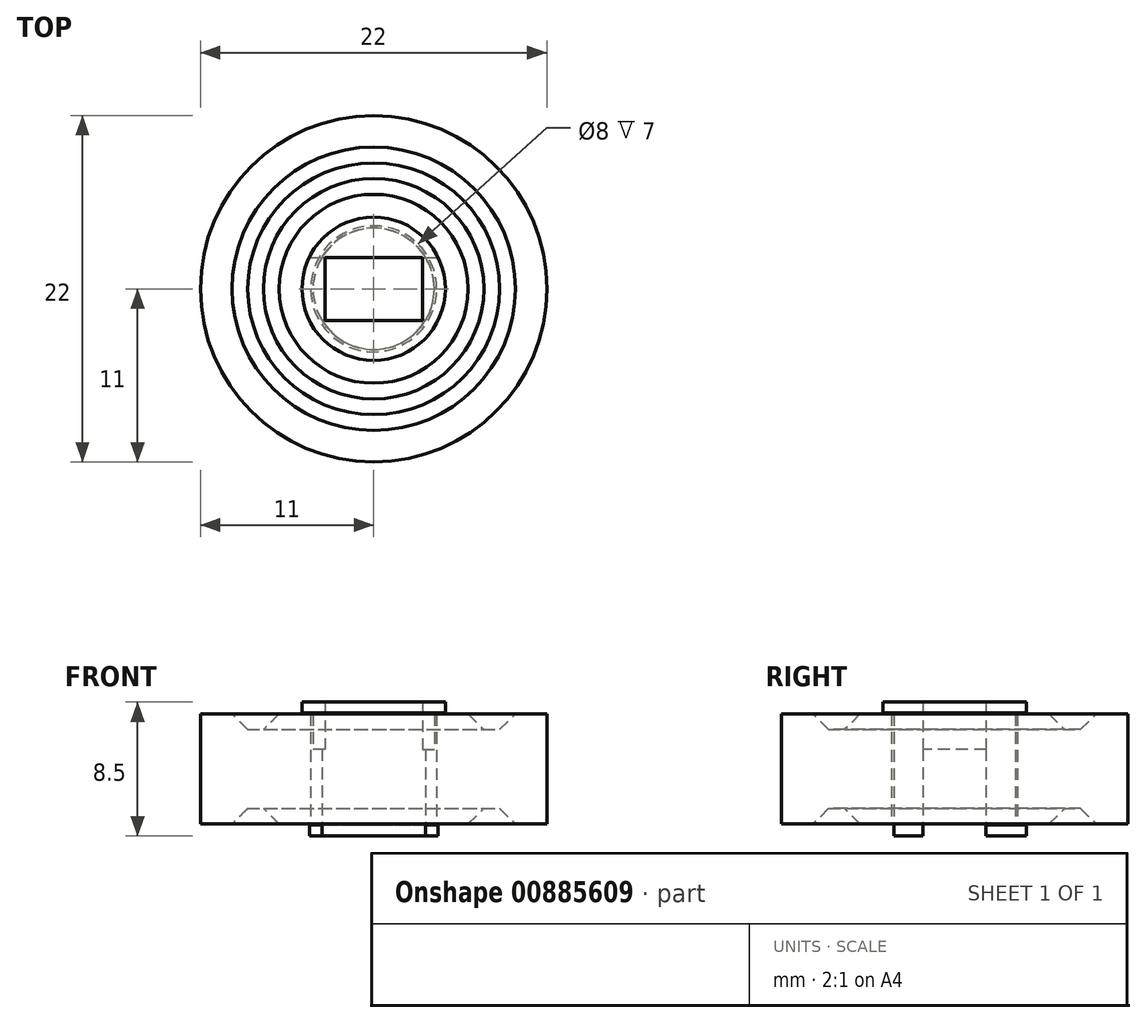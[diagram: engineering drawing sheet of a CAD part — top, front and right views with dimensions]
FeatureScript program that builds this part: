
annotation { "Feature Type Name" : "Feature", "Feature Type Description" : "" }
export const myFeature = defineFeature(function(context is Context, id is Id, definition is map)
    precondition{}
    {
        {
            assignVariable(context, id + "F0", {"name" : "bearing_thick", "anyValue" : 7});
        }
        {
            var Q0;
            Q0=qCreatedBy(makeId("Right.planeOp"),FACE);
            var sketch = newSketch(context, id + "F1", { "sketchPlane" : qUnion([Q0])});
            skLineSegment(sketch, "E0.bottom", {"start": v(-4, 0) * mm, "end": v(-11, 0) * mm});
            skLineSegment(sketch, "E0.top", {"start": v(-4, 3.5) * mm, "end": v(-6, 3.5) * mm});
            skLineSegment(sketch, "E0.left", {"start": v(-4, 0) * mm, "end": v(-4, 3.5) * mm});
            skLineSegment(sketch, "E0.right", {"start": v(-11, 0) * mm, "end": v(-11, 3.5) * mm});
            skLineSegment(sketch, "E1", {"start": v(-9, 3.5) * mm, "end": v(-8, 2.5) * mm});
            skLineSegment(sketch, "E2", {"start": v(-8, 2.5) * mm, "end": v(-7, 2.5) * mm});
            skLineSegment(sketch, "E3", {"start": v(-7, 2.5) * mm, "end": v(-6, 3.5) * mm});
            skLineSegment(sketch, "E4.MirrorCS", {"start": v(7, 2.5) * mm, "end": v(6, 3.5) * mm});
            skLineSegment(sketch, "E5.MirrorCS", {"start": v(4, 0) * mm, "end": v(4, 3.5) * mm});
            skLineSegment(sketch, "E6.MirrorCS", {"start": v(11, 0) * mm, "end": v(11, 3.5) * mm});
            skLineSegment(sketch, "E7.MirrorCS", {"start": v(9, 3.5) * mm, "end": v(8, 2.5) * mm});
            skLineSegment(sketch, "E8.MirrorCS", {"start": v(4, 0) * mm, "end": v(11, 0) * mm});
            skLineSegment(sketch, "E9.MirrorCS", {"start": v(4, 3.5) * mm, "end": v(6, 3.5) * mm});
            skLineSegment(sketch, "E10.MirrorCS", {"start": v(8, 2.5) * mm, "end": v(7, 2.5) * mm});
            skLineSegment(sketch, "E11.trimOffspring", {"start": v(-9, 3.5) * mm, "end": v(-11, 3.5) * mm});
            skLineSegment(sketch, "E12.trimOffspring", {"start": v(9, 3.5) * mm, "end": v(11, 3.5) * mm});
            skLineSegment(sketch, "E13", {"start": v(0, 0) * mm, "end": v(0, 4.43) * mm});
            skSolve(sketch);
        }
        {
            var Q0;
            Q0=makeQuery(id+"F1.imprint","IMPRINT",FACE,{"disambiguationData":[TD([[makeQuery(id+"F1.imprint","IMPRINT",EDGE,{"derivedFrom":sQuery(id+"F1.wireOp",EDGE,"E0.bottom")}),-1.0]])]});
            var Q1;
            Q1=makeQuery(id+"F1.imprint","IMPRINT",FACE,{"disambiguationData":[TD([[makeQuery(id+"F1.imprint","IMPRINT",EDGE,{"derivedFrom":sQuery(id+"F1.wireOp",EDGE,"E4.MirrorCS")}),1.0]])]});
            var Q2;
            Q2=sQuery(id+"F1.wireOp",EDGE,"E13");
            revolve(context, id + "F2", {"surfaceOperationType" : NewSurfaceOperationType.NEW, "entities" : qUnion([Q0, Q1]), "axis" : qUnion([Q2]), "revolveType" : RevolveType.FULL});
        }
        {
            var Q0;
            Q0=makeQuery(id+"F2.opRevolve","SWEPT_BODY",BODY,{"disambiguationData":[OSD([sQuery(id+"F1.wireOp",EDGE,"E0.bottom"),sQuery(id+"F1.wireOp",EDGE,"E0.top"),sQuery(id+"F1.wireOp",EDGE,"E0.left"),sQuery(id+"F1.wireOp",EDGE,"E0.right"),sQuery(id+"F1.wireOp",EDGE,"E1"),sQuery(id+"F1.wireOp",EDGE,"E2"),sQuery(id+"F1.wireOp",EDGE,"E3"),sQuery(id+"F1.wireOp",EDGE,"E11.trimOffspring")])]});
            var Q1;
            Q1=makeQuery(id+"F2.opRevolve","SWEPT_BODY",BODY,{"disambiguationData":[OSD([sQuery(id+"F1.wireOp",EDGE,"E4.MirrorCS"),sQuery(id+"F1.wireOp",EDGE,"E5.MirrorCS"),sQuery(id+"F1.wireOp",EDGE,"E6.MirrorCS"),sQuery(id+"F1.wireOp",EDGE,"E7.MirrorCS"),sQuery(id+"F1.wireOp",EDGE,"E8.MirrorCS"),sQuery(id+"F1.wireOp",EDGE,"E9.MirrorCS"),sQuery(id+"F1.wireOp",EDGE,"E10.MirrorCS"),sQuery(id+"F1.wireOp",EDGE,"E12.trimOffspring")])]});
            var Q2;
            Q2=qCreatedBy(makeId("Top.planeOp"),FACE);
            mirror(context, id + "F3", {"entities" : qUnion([Q0, Q1]), "mirrorPlane" : qUnion([Q2])});
        }
        {
            var Q0;
            Q0=qCreatedBy(makeId("Top.planeOp"),FACE);
            var sketch = newSketch(context, id + "F4", { "sketchPlane" : qUnion([Q0])});
            skCircle(sketch, "E14", {"center": v(0, 0) * mm, "radius": 3.85 * mm});
            skLineSegment(sketch, "E15.bottom", {"start": v(-3.1, 2) * mm, "end": v(3.1, 2) * mm});
            skLineSegment(sketch, "E15.top", {"start": v(-3.1, -2) * mm, "end": v(3.1, -2) * mm});
            skLineSegment(sketch, "E15.left", {"start": v(-3.1, 2) * mm, "end": v(-3.1, -2) * mm});
            skLineSegment(sketch, "E15.right", {"start": v(3.1, 2) * mm, "end": v(3.1, -2) * mm});
            skSolve(sketch);
        }
        {
            var Q0;
            Q0=makeQuery(id+"F3.opPattern","COPY",BODY,{"derivedFrom":makeQuery(id+"F2.opRevolve","SWEPT_BODY",BODY,{"disambiguationData":[OSD([sQuery(id+"F1.wireOp",EDGE,"E4.MirrorCS"),sQuery(id+"F1.wireOp",EDGE,"E5.MirrorCS"),sQuery(id+"F1.wireOp",EDGE,"E6.MirrorCS"),sQuery(id+"F1.wireOp",EDGE,"E7.MirrorCS"),sQuery(id+"F1.wireOp",EDGE,"E8.MirrorCS"),sQuery(id+"F1.wireOp",EDGE,"E9.MirrorCS"),sQuery(id+"F1.wireOp",EDGE,"E10.MirrorCS"),sQuery(id+"F1.wireOp",EDGE,"E12.trimOffspring")])]}),"instanceName":"1"});
            deleteBodies(context, id + "F5", {"entities" : qUnion([Q0])});
        }
        {
            var Q0;
            Q0=makeQuery(id+"F3.opPattern","COPY",BODY,{"derivedFrom":makeQuery(id+"F2.opRevolve","SWEPT_BODY",BODY,{"disambiguationData":[OSD([sQuery(id+"F1.wireOp",EDGE,"E0.bottom"),sQuery(id+"F1.wireOp",EDGE,"E0.top"),sQuery(id+"F1.wireOp",EDGE,"E0.left"),sQuery(id+"F1.wireOp",EDGE,"E0.right"),sQuery(id+"F1.wireOp",EDGE,"E1"),sQuery(id+"F1.wireOp",EDGE,"E2"),sQuery(id+"F1.wireOp",EDGE,"E3"),sQuery(id+"F1.wireOp",EDGE,"E11.trimOffspring")])]}),"instanceName":"1"});
            deleteBodies(context, id + "F6", {"entities" : qUnion([Q0])});
        }
        {
            var Q0;
            Q0=makeQuery(id+"F2.opRevolve","SWEPT_BODY",BODY,{"disambiguationData":[OSD([sQuery(id+"F1.wireOp",EDGE,"E4.MirrorCS"),sQuery(id+"F1.wireOp",EDGE,"E5.MirrorCS"),sQuery(id+"F1.wireOp",EDGE,"E6.MirrorCS"),sQuery(id+"F1.wireOp",EDGE,"E7.MirrorCS"),sQuery(id+"F1.wireOp",EDGE,"E8.MirrorCS"),sQuery(id+"F1.wireOp",EDGE,"E9.MirrorCS"),sQuery(id+"F1.wireOp",EDGE,"E10.MirrorCS"),sQuery(id+"F1.wireOp",EDGE,"E12.trimOffspring")])]});
            deleteBodies(context, id + "F7", {"entities" : qUnion([Q0])});
        }
        {
            var Q0;
            Q0=makeQuery(id+"F2.opRevolve","SWEPT_BODY",BODY,{"disambiguationData":[OSD([sQuery(id+"F1.wireOp",EDGE,"E0.bottom"),sQuery(id+"F1.wireOp",EDGE,"E0.top"),sQuery(id+"F1.wireOp",EDGE,"E0.left"),sQuery(id+"F1.wireOp",EDGE,"E0.right"),sQuery(id+"F1.wireOp",EDGE,"E1"),sQuery(id+"F1.wireOp",EDGE,"E2"),sQuery(id+"F1.wireOp",EDGE,"E3"),sQuery(id+"F1.wireOp",EDGE,"E11.trimOffspring")])]});
            var Q1;
            Q1=qCreatedBy(makeId("Top.planeOp"),FACE);
            mirror(context, id + "F8", {"operationType" : NewBodyOperationType.ADD, "entities" : qUnion([Q0]), "mirrorPlane" : qUnion([Q1])});
        }
        {
            var Q0;
            Q0=makeQuery(id+"F4.imprint","IMPRINT",FACE,{"disambiguationData":[TD([[makeQuery(id+"F4.imprint","IMPRINT",EDGE,{"derivedFrom":sQuery(id+"F4.wireOp",EDGE,"E14")}),1.0]])]});
            extrude(context, id + "F9", {"entities" : qUnion([Q0]), "depth" : (getVariable(context, 'bearing_thick') + 1.5) * mm, "offsetDistance" : 25 * mm, "symmetric" : true});
        }
        {
            var Q0;
            Q0=makeQuery(id+"F9.opExtrude","CAP_FACE",FACE,{"disambiguationData":[OSD([sQuery(id+"F4.wireOp",EDGE,"E14"),sQuery(id+"F4.wireOp",EDGE,"E15.bottom"),sQuery(id+"F4.wireOp",EDGE,"E15.top"),sQuery(id+"F4.wireOp",EDGE,"E15.left"),sQuery(id+"F4.wireOp",EDGE,"E15.right")])],"isStart":true});
            var sketch = newSketch(context, id + "F10", { "sketchPlane" : qUnion([Q0])});
            skLineSegment(sketch, "E16", {"start": v(-3.1, 2) * mm, "end": v(-3.29, 2) * mm});
            skLineSegment(sketch, "E17", {"start": v(-3.1, -2) * mm, "end": v(-3.29, -2) * mm});
            skLineSegment(sketch, "E18", {"start": v(-3.1, 2) * mm, "end": v(-3.1, -2) * mm});
            skLineSegment(sketch, "E19.MirrorCS", {"start": v(3.1, -2) * mm, "end": v(3.29, -2) * mm});
            skLineSegment(sketch, "E20.MirrorCS", {"start": v(3.1, 2) * mm, "end": v(3.1, -2) * mm});
            skLineSegment(sketch, "E21.MirrorCS", {"start": v(3.1, 2) * mm, "end": v(3.29, 2) * mm});
            skSolve(sketch);
        }
        {
            var Q0;
            {var subQ0=sQuery(id+"F10.wireOp",EDGE,"E16");Q0=makeQuery(id+"F10.imprint","IMPRINT",FACE,{"disambiguationData":[TD([[makeQuery(id+"F10.imprint","IMPRINT",EDGE,{"derivedFrom":subQ0}),1.0]])]});}
            var Q1;
            {var subQ0=sQuery(id+"F10.wireOp",EDGE,"E19.MirrorCS");Q1=makeQuery(id+"F10.imprint","IMPRINT",FACE,{"disambiguationData":[TD([[makeQuery(id+"F10.imprint","IMPRINT",EDGE,{"derivedFrom":subQ0}),1.0]])]});}
            extrude(context, id + "F11", {"entities" : qUnion([Q0, Q1]), "operationType" : NewBodyOperationType.REMOVE, "oppositeDirection" : true, "depth" : ((getVariable(context, 'bearing_thick') + 4) / 2) * mm, "offsetDistance" : 25 * mm});
        }
        {
            var Q0;
            {var subQ0=sQuery(id+"F4.wireOp",EDGE,"E14");var subQ1=sQuery(id+"F4.wireOp",EDGE,"E15.top");Q0=makeQuery(id+"F11.boolean.opBoolean","SPLIT",FACE,{"disambiguationData":[TD([makeQuery(id+"F9.opExtrude","SWEPT_FACE",FACE,{"disambiguationData":[OSD([subQ1])]})])],"derivedFrom":makeQuery(id+"F9.opExtrude","CAP_FACE",FACE,{"disambiguationData":[OSD([subQ0,sQuery(id+"F4.wireOp",EDGE,"E15.bottom"),subQ1,sQuery(id+"F4.wireOp",EDGE,"E15.left"),sQuery(id+"F4.wireOp",EDGE,"E15.right")])],"isStart":true})});}
            var sketch = newSketch(context, id + "F12", { "sketchPlane" : qUnion([Q0])});
            skArc(sketch, "E22.0", {"start": v(-4.09, 2) * mm, "mid": v(0, 4.55) * mm, "end": v(4.09, 2) * mm});
            skLineSegment(sketch, "E23", {"start": v(-4.09, 2) * mm, "end": v(-3.29, 2) * mm});
            skLineSegment(sketch, "E24", {"start": v(3.29, 2) * mm, "end": v(4.09, 2) * mm});
            skArc(sketch, "E25.MirrorCS", {"start": v(-4.09, -2) * mm, "mid": v(0, -4.55) * mm, "end": v(4.09, -2) * mm});
            skLineSegment(sketch, "E26.MirrorCS", {"start": v(-4.09, -2) * mm, "end": v(-3.29, -2) * mm});
            skLineSegment(sketch, "E27.MirrorCS", {"start": v(3.29, -2) * mm, "end": v(4.09, -2) * mm});
            skArc(sketch, "E28", {"start": v(-3.29, -2) * mm, "mid": v(0, -3.85) * mm, "end": v(3.29, -2) * mm});
            skArc(sketch, "E29.trimOffspring", {"start": v(3.29, 2) * mm, "mid": v(0, 3.85) * mm, "end": v(-3.29, 2) * mm});
            skSolve(sketch);
        }
        {
            var Q0;
            Q0=makeQuery(id+"F12.imprint","IMPRINT",FACE,{"disambiguationData":[TD([[makeQuery(id+"F12.imprint","IMPRINT",EDGE,{"derivedFrom":sQuery(id+"F12.wireOp",EDGE,"E25.MirrorCS")}),1.0]])]});
            var Q1;
            Q1=makeQuery(id+"F12.imprint","IMPRINT",FACE,{"disambiguationData":[TD([[makeQuery(id+"F12.imprint","IMPRINT",EDGE,{"derivedFrom":sQuery(id+"F12.wireOp",EDGE,"E22.0")}),-1.0]])]});
            extrude(context, id + "F13", {"entities" : qUnion([Q0, Q1]), "operationType" : NewBodyOperationType.ADD, "oppositeDirection" : true, "depth" : 0.7 * mm, "offsetDistance" : 25 * mm});
        }
        {
            var Q0;
            Q0=makeQuery(id+"F9.opExtrude","CAP_FACE",FACE,{"disambiguationData":[OSD([sQuery(id+"F4.wireOp",EDGE,"E14"),sQuery(id+"F4.wireOp",EDGE,"E15.bottom"),sQuery(id+"F4.wireOp",EDGE,"E15.top"),sQuery(id+"F4.wireOp",EDGE,"E15.left"),sQuery(id+"F4.wireOp",EDGE,"E15.right")])],"isStart":false});
            var sketch = newSketch(context, id + "F14", { "sketchPlane" : qUnion([Q0])});
            skCircle(sketch, "E30", {"center": v(0, 0) * mm, "radius": 4.55 * mm});
            skSolve(sketch);
        }
        {
            var Q0;
            Q0=makeQuery(id+"F14.imprint","IMPRINT",FACE,{"disambiguationData":[TD([[makeQuery(id+"F14.imprint","IMPRINT",EDGE,{"derivedFrom":sQuery(id+"F14.wireOp",EDGE,"E30")}),1.0]])]});
            extrude(context, id + "F15", {"entities" : qUnion([Q0]), "operationType" : NewBodyOperationType.ADD, "oppositeDirection" : true, "depth" : 0.7 * mm, "offsetDistance" : 25 * mm});
        }
    });
